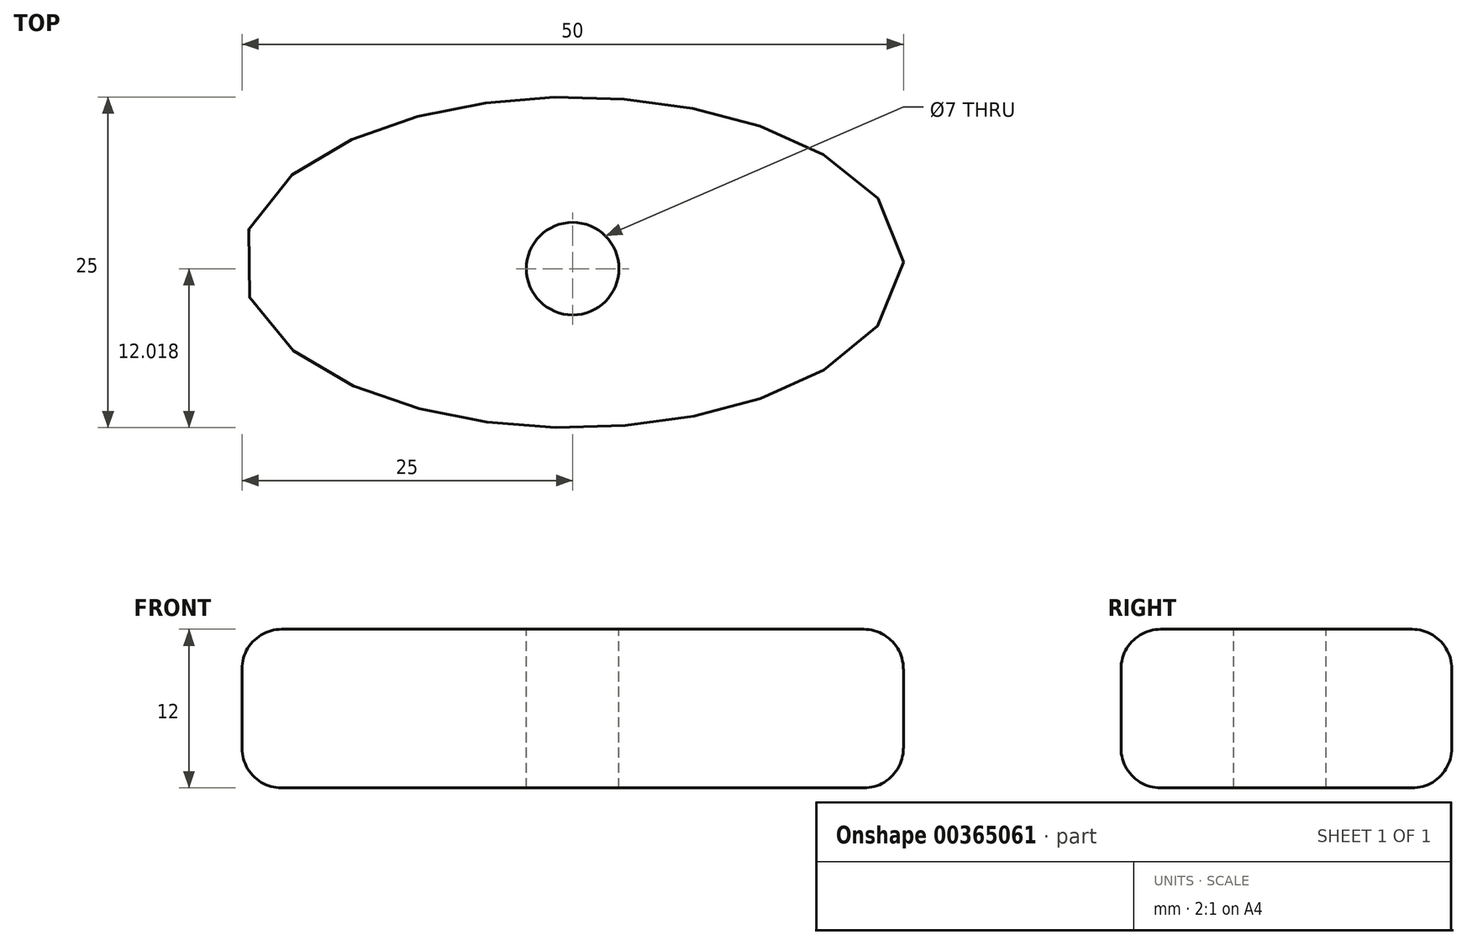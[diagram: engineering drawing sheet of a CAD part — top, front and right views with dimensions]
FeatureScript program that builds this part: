
annotation { "Feature Type Name" : "Feature", "Feature Type Description" : "" }
export const myFeature = defineFeature(function(context is Context, id is Id, definition is map)
    precondition{}
    {
        {
            var Q0;
            Q0=qCreatedBy(makeId("Top.planeOp"),FACE);
            var sketch = newSketch(context, id + "F0", { "sketchPlane" : qUnion([Q0])});
            skEllipse(sketch, "E0", {"center": v(0, 0) * mm, "majorRadius": 25 * mm, "minorRadius": 12.5 * mm, "majorAxis": v(1, 0)});
            skCircle(sketch, "E1", {"center": v(0, 0) * mm, "radius": 11 * mm});
            skCircle(sketch, "E2", {"center": v(0, -0.48) * mm, "radius": 3.5 * mm});
            skSolve(sketch);
        }
        {
            var Q0;
            Q0=makeQuery(id+"F0.imprint","IMPRINT",FACE,{"disambiguationData":[TD([[makeQuery(id+"F0.imprint","IMPRINT",EDGE,{"derivedFrom":sQuery(id+"F0.wireOp",EDGE,"E0")}),1.0]])]});
            var Q1;
            Q1=makeQuery(id+"F0.imprint","IMPRINT",FACE,{"disambiguationData":[TD([[makeQuery(id+"F0.imprint","IMPRINT",EDGE,{"derivedFrom":sQuery(id+"F0.wireOp",EDGE,"E1")}),1.0]])]});
            extrude(context, id + "F1", {"entities" : qUnion([Q0, Q1]), "oppositeDirection" : true, "depth" : 2 * mm});
        }
        {
            var Q0;
            Q0=makeQuery(id+"F1.opExtrude","CAP_FACE",FACE,{"disambiguationData":[OSD([sQuery(id+"F0.wireOp",EDGE,"E0"),sQuery(id+"F0.wireOp",EDGE,"E2")])],"isStart":true});
            var sketch = newSketch(context, id + "F2", { "sketchPlane" : qUnion([Q0])});
            skCircle(sketch, "E3", {"center": v(0, 0) * mm, "radius": 11 * mm});
            skSolve(sketch);
        }
        {
            var Q0;
            Q0=makeQuery(id+"F2.imprint","IMPRINT",FACE,{"disambiguationData":[TD([[makeQuery(id+"F2.imprint","IMPRINT",EDGE,{"derivedFrom":sQuery(id+"F2.wireOp",EDGE,"E3")}),-1.0]])]});
            var Q1;
            Q1=makeQuery(id+"F1.opExtrude","CAP_FACE",FACE,{"disambiguationData":[OSD([sQuery(id+"F0.wireOp",EDGE,"E0"),sQuery(id+"F0.wireOp",EDGE,"E2")])],"isStart":true});
            var Q2;
            Q2=makeQuery(id+"F1.opExtrude","CAP_FACE",FACE,{"disambiguationData":[OSD([sQuery(id+"F0.wireOp",EDGE,"E0"),sQuery(id+"F0.wireOp",EDGE,"E2")])],"isStart":false});
            extrude(context, id + "F3", {"entities" : qUnion([Q0, Q1, Q2]), "operationType" : NewBodyOperationType.ADD, "depth" : 10 * mm});
        }
        {
            var Q0;
            Q0=makeQuery(id+"F1.opExtrude","CAP_EDGE",EDGE,{"disambiguationData":[OSD([sQuery(id+"F0.wireOp",EDGE,"E0")])],"isStart":false});
            var Q1;
            {var subQ0=sQuery(id+"F0.wireOp",EDGE,"E0");Q1=makeQuery(id+"F3.opExtrude","CAP_EDGE",EDGE,{"disambiguationData":[OSD([subQ0]),TDD([makeQuery(id+"F1.opExtrude","CAP_EDGE",EDGE,{"disambiguationData":[OSD([subQ0])],"isStart":true})])],"isStart":false});}
            fillet(context, id + "F4", {"entities" : qUnion([Q0, Q1]), "radius" : 3 * mm, "tangentPropagation" : true, "allowEdgeOverflow" : false});
        }
    });
